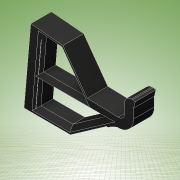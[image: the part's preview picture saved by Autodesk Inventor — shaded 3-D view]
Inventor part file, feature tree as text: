
AUTODESK INVENTOR PART (.ipt)
format: ipt  version: 2017 (Build 210142000, 142)  size: 215,040 bytes
history: native  units: in
note: dims shown in document units (in); Inventor stores cm internally (conversion verified against a paired STEP export)
features: extrude x2, sketch x2, plane x1, chamfer x1
ambient origin geometry x8: Origin, YZ Plane, XZ Plane, XY Plane, X Axis, Y Axis, Z Axis, Center Point
bodies: Solid1 (feature_tree)
feature tree (6):
  extrude  "Extrusion1"  Depth=0.2in
  plane  "Work Plane1"
  extrude  "Extrusion2"  Depth=0.35in TaperAngle=0.0deg
  chamfer  "Chamfer3"  Distance=1.5in
  sketch  "Sketch1"  dims[d3=0.2in d6=0.0344in]
  sketch  "Sketch2"  dims[d7=0.6in d8=0.0in d24=1.0in d25=0.0in d27=0.5in d28=0.2165in d29=0.2165in d30=0.0787in d31=0.0787in d32=0.0079in d33=1.0651in d34=1.0651in d36=0.9in d37=1.5in d39=2.38in d40=0.754in d41=0.446in d42=0.2715in d43=0.1849in d44=0.2715in d45=0.1825in d46=0.2in d47=180.0deg d48=90.0deg d51=0.25in d52=1.0in d53=0.0in d54=0.015in d55=0.175in d56=0.175in d57=0.175in d58=0.175in d59=0.35in d60=0.35in d67=0.3in d68=0.125in d69=0.125in d70=45.0deg]
